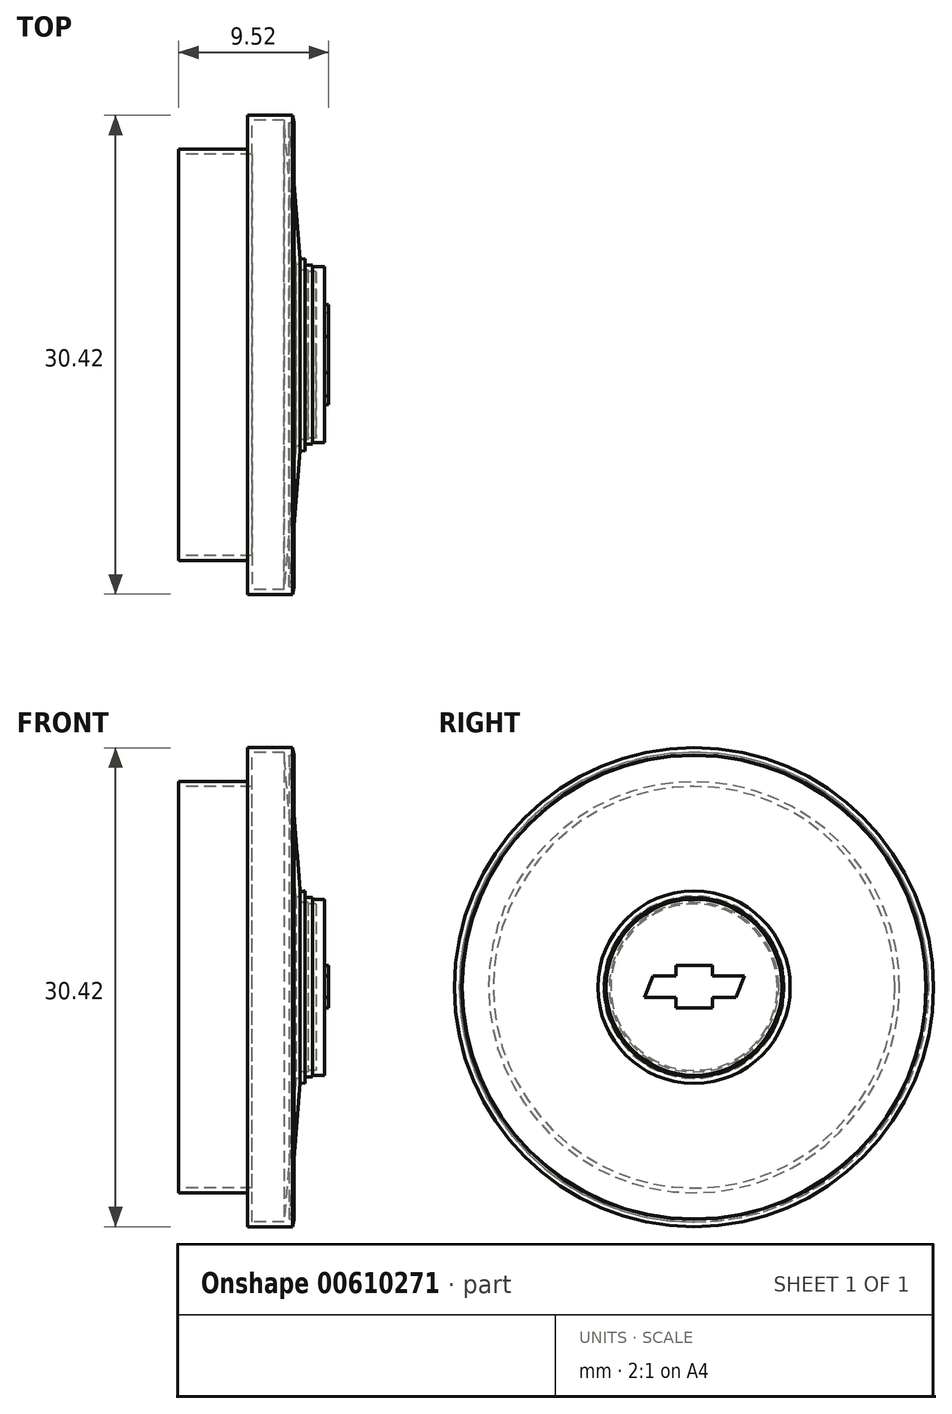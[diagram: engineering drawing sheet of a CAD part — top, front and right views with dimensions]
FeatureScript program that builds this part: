
annotation { "Feature Type Name" : "Feature", "Feature Type Description" : "" }
export const myFeature = defineFeature(function(context is Context, id is Id, definition is map)
    precondition{}
    {
        {
            var Q0;
            Q0=qCreatedBy(makeId("Front.planeOp"),FACE);
            var sketch = newSketch(context, id + "F0", { "sketchPlane" : qUnion([Q0])});
            skLineSegment(sketch, "E0", {"start": v(-5.5, 0) * mm, "end": v(3.5, 0) * mm});
            skLineSegment(sketch, "E1", {"start": v(3.5, 0) * mm, "end": v(3.5, 5.59) * mm});
            skLineSegment(sketch, "E2", {"start": v(1.71, 15.21) * mm, "end": v(-1.14, 15.21) * mm});
            skLineSegment(sketch, "E3", {"start": v(-1.14, 15.21) * mm, "end": v(-1.14, 13.06) * mm});
            skLineSegment(sketch, "E4", {"start": v(-1.14, 13.06) * mm, "end": v(-5.5, 13.06) * mm});
            skLineSegment(sketch, "E5", {"start": v(-5.5, 13.06) * mm, "end": v(-5.5, 0) * mm});
            skLineSegment(sketch, "E6", {"start": v(3.5, 5.59) * mm, "end": v(3, 5.59) * mm});
            skLineSegment(sketch, "E7", {"start": v(3, 5.59) * mm, "end": v(3, 5.69) * mm});
            skLineSegment(sketch, "E8", {"start": v(3, 5.69) * mm, "end": v(2.52, 5.69) * mm});
            skLineSegment(sketch, "E9", {"start": v(2.52, 5.69) * mm, "end": v(2.52, 6.1) * mm});
            skLineSegment(sketch, "E10", {"start": v(2.52, 6.1) * mm, "end": v(2.21, 6.08) * mm});
            skLineSegment(sketch, "E11", {"start": v(2.21, 6.08) * mm, "end": v(1.5, 14.73) * mm});
            skLineSegment(sketch, "E12", {"start": v(1.5, 14.73) * mm, "end": v(1.82, 14.75) * mm});
            skLineSegment(sketch, "E13", {"start": v(1.82, 14.75) * mm, "end": v(1.71, 15.21) * mm});
            skSolve(sketch);
        }
        {
            var Q0;
            Q0 = qSketchRegion(id + "F0", true);
            var Q1;
            Q1 = qSketchRegion(id + "FX202QDPRsENXMe_1", true);
            var Q2;
            Q2=sQuery(id+"F0.wireOp",EDGE,"E0");
            revolve(context, id + "F1", {"entities" : qUnion([Q0, Q1]), "axis" : qUnion([Q2]), "revolveType" : RevolveType.FULL});
        }
        {
            var Q0;
            Q0=makeQuery(id+"F1.opRevolve","SWEPT_FACE",FACE,{"disambiguationData":[OSD([sQuery(id+"F0.wireOp",EDGE,"E5")])]});
            shell(context, id + "F2", {"entities" : qUnion([Q0]), "thickness" : .3 * mm});
        }
        {
            var Q0;
            Q0=makeQuery(id+"F1.opRevolve","SWEPT_FACE",FACE,{"disambiguationData":[OSD([sQuery(id+"F0.wireOp",EDGE,"E1")])]});
            var sketch = newSketch(context, id + "F3", { "sketchPlane" : qUnion([Q0])});
            skLineSegment(sketch, "E14", {"start": v(-1.13, 1.38) * mm, "end": v(1.16, 1.38) * mm});
            skLineSegment(sketch, "E15", {"start": v(1.16, 1.38) * mm, "end": v(1.16, 0.7) * mm});
            skLineSegment(sketch, "E16", {"start": v(1.16, 0.7) * mm, "end": v(3.2, 0.7) * mm});
            skLineSegment(sketch, "E17", {"start": v(3.2, 0.7) * mm, "end": v(2.65, -0.65) * mm});
            skLineSegment(sketch, "E18", {"start": v(2.65, -0.65) * mm, "end": v(1.16, -0.65) * mm});
            skLineSegment(sketch, "E19", {"start": v(1.16, -0.65) * mm, "end": v(1.16, -1.32) * mm});
            skLineSegment(sketch, "E20", {"start": v(1.16, -1.32) * mm, "end": v(-1.13, -1.32) * mm});
            skLineSegment(sketch, "E21", {"start": v(-1.13, -1.32) * mm, "end": v(-1.13, -0.65) * mm});
            skLineSegment(sketch, "E22", {"start": v(-1.13, -0.65) * mm, "end": v(-3.16, -0.65) * mm});
            skLineSegment(sketch, "E23", {"start": v(-3.16, -0.65) * mm, "end": v(-2.62, 0.7) * mm});
            skLineSegment(sketch, "E24", {"start": v(-2.62, 0.7) * mm, "end": v(-1.13, 0.7) * mm});
            skLineSegment(sketch, "E25", {"start": v(-1.13, 0.7) * mm, "end": v(-1.13, 1.38) * mm});
            skCircle(sketch, "E26", {"center": v(0, 0) * mm, "radius": 4.9 * mm});
            skSolve(sketch);
        }
        {
            var Q0;
            Q0=makeQuery(id+"F3.imprint","IMPRINT",FACE,{"disambiguationData":[TD([[makeQuery(id+"F3.imprint","IMPRINT",EDGE,{"derivedFrom":sQuery(id+"F3.wireOp",EDGE,"E14")}),-1.0]])]});
            extrude(context, id + "F4", {"entities" : qUnion([Q0]), "operationType" : NewBodyOperationType.ADD, "depth" : .5 * mm, "offsetDistance" : 25.4 * mm});
        }
        {
            var Q0;
            Q0 = qSketchRegion(id + "F3", true);
            var Q1;
            Q1=makeQuery(id+"F1.opRevolve","SWEPT_FACE",FACE,{"disambiguationData":[OSD([sQuery(id+"F0.wireOp",EDGE,"E1")])]});
            extrude(context, id + "F5", {"entities" : qUnion([Q0, Q1]), "operationType" : NewBodyOperationType.ADD, "depth" : 0.25 * mm, "offsetDistance" : 25.4 * mm});
        }
    });
